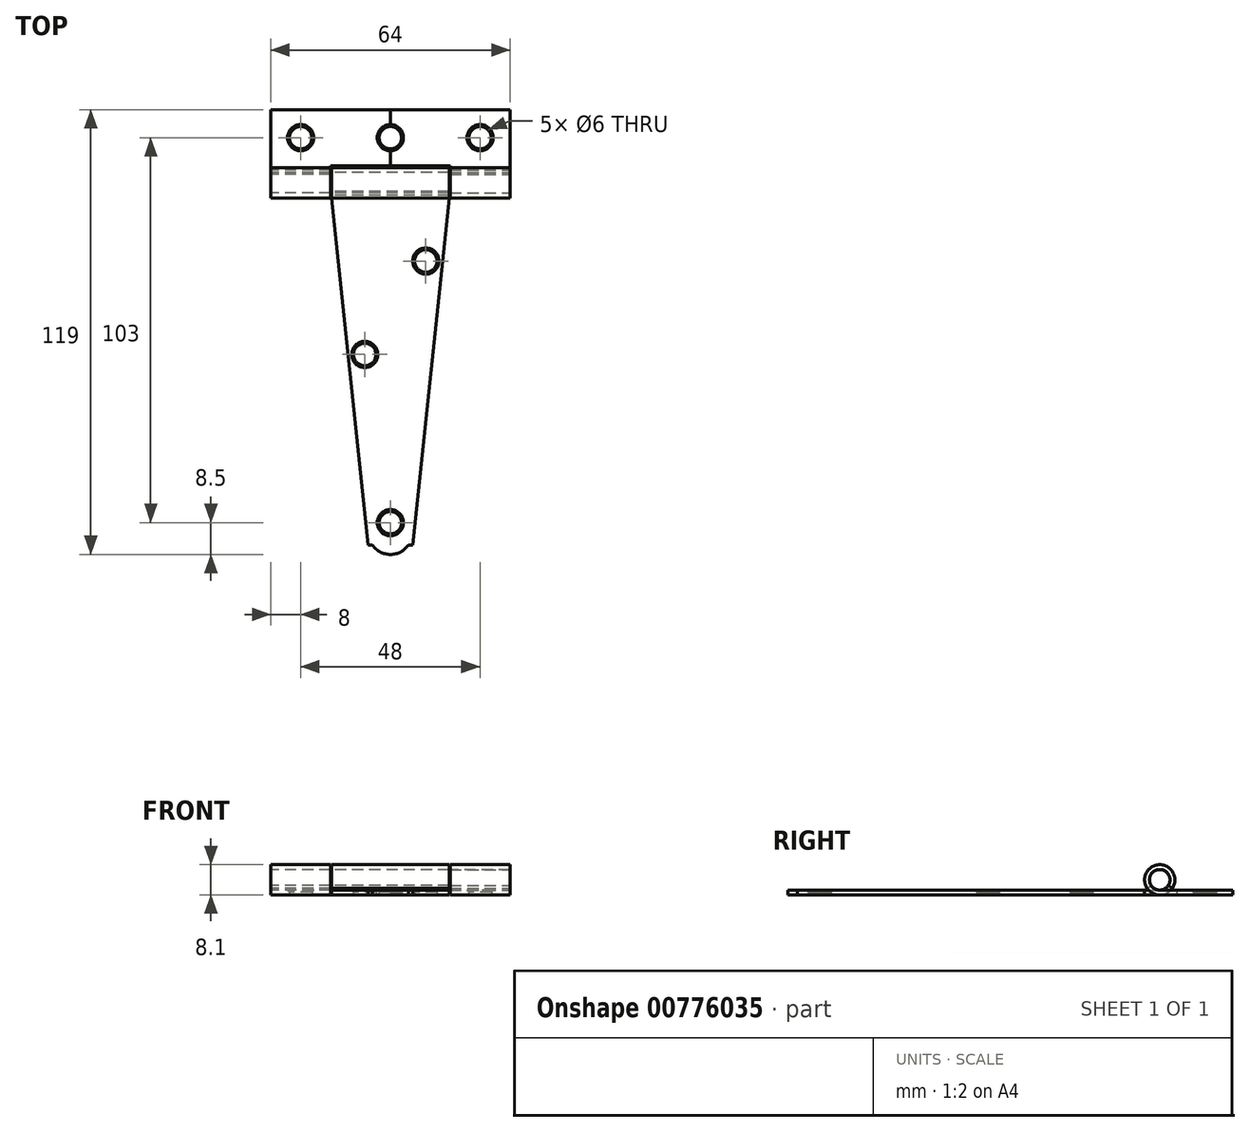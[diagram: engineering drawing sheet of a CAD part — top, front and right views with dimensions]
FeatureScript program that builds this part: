
annotation { "Feature Type Name" : "Feature", "Feature Type Description" : "" }
export const myFeature = defineFeature(function(context is Context, id is Id, definition is map)
    precondition{}
    {
        {
            var Q0;
            Q0=qCreatedBy(makeId("Top.planeOp"),FACE);
            var sketch = newSketch(context, id + "F0", { "sketchPlane" : qUnion([Q0])});
            skLineSegment(sketch, "E0.bottom", {"start": v(-32, 15.5) * mm, "end": v(0, 15.5) * mm});
            skLineSegment(sketch, "E0.top", {"start": v(-32, 0) * mm, "end": v(-16, 0) * mm});
            skLineSegment(sketch, "E0.left", {"start": v(-32, 15.5) * mm, "end": v(-32, 0) * mm});
            skLineSegment(sketch, "E0.right", {"start": v(0, 15.5) * mm, "end": v(0, 11) * mm});
            skLineSegment(sketch, "E1", {"start": v(0, 0.5) * mm, "end": v(-16, 0.5) * mm});
            skLineSegment(sketch, "E2", {"start": v(-16, 0.5) * mm, "end": v(-16, 0) * mm});
            skPoint(sketch, "E3.orphan", {"position": v(0, 0) * mm});
            skArc(sketch, "E4", {"start": v(0, 11) * mm, "mid": v(-3, 8) * mm, "end": v(0, 5) * mm});
            skCircle(sketch, "E5", {"center": v(-24, 8) * mm, "radius": 3 * mm});
            skLineSegment(sketch, "E6", {"start": v(-32, 0) * mm, "end": v(-32, -8.1) * mm, "construction": true});
            skLineSegment(sketch, "E7", {"start": v(-32, -8.1) * mm, "end": v(-16, -8.1) * mm, "construction": true});
            skLineSegment(sketch, "E8", {"start": v(-16, -8.1) * mm, "end": v(-16, 0) * mm, "construction": true});
            skLineSegment(sketch, "E9.trimOffspring", {"start": v(0, 5) * mm, "end": v(0, 0.5) * mm});
            skLineSegment(sketch, "E10", {"start": v(0, 0) * mm, "end": v(-15.75, 0) * mm, "construction": true});
            skLineSegment(sketch, "E11", {"start": v(-15.75, 0) * mm, "end": v(-15.75, -8.1) * mm, "construction": true});
            skLineSegment(sketch, "E12", {"start": v(-15.75, -8.1) * mm, "end": v(0, -8.1) * mm, "construction": true});
            skLineSegment(sketch, "E13", {"start": v(0, -8.1) * mm, "end": v(0, 0) * mm, "construction": true});
            skLineSegment(sketch, "E14", {"start": v(-15.75, -8.1) * mm, "end": v(-6, -101) * mm});
            skLineSegment(sketch, "E15", {"start": v(-6, -101) * mm, "end": v(-4.81, -101) * mm});
            skLineSegment(sketch, "E16", {"start": v(0, 0.5) * mm, "end": v(0, -103.5) * mm});
            skArc(sketch, "E17", {"start": v(-4.81, -101) * mm, "mid": v(-2.71, -102.84) * mm, "end": v(0, -103.5) * mm});
            skCircle(sketch, "E18", {"center": v(0, -95) * mm, "radius": 3 * mm});
            skCircle(sketch, "E19", {"center": v(-6.85, -50) * mm, "radius": 3 * mm});
            skCircle(sketch, "E20", {"center": v(9.48, -25) * mm, "radius": 3 * mm});
            skLineSegment(sketch, "E21", {"start": v(-15.75, -8.1) * mm, "end": v(0, -8.1) * mm});
            skLineSegment(sketch, "E22", {"start": v(-6.85, -50) * mm, "end": v(-11.35, -50) * mm, "construction": true});
            skLineSegment(sketch, "E23.MirrorCS", {"start": v(15.75, -8.1) * mm, "end": v(6, -101) * mm});
            skLineSegment(sketch, "E24", {"start": v(9.48, -25) * mm, "end": v(13.98, -25) * mm, "construction": true});
            skSolve(sketch);
        }
        {
            var Q0;
            Q0=makeQuery(id+"F0.imprint","IMPRINT",FACE,{"disambiguationData":[TD([[makeQuery(id+"F0.imprint","IMPRINT",EDGE,{"derivedFrom":sQuery(id+"F0.wireOp",EDGE,"E0.bottom")}),-1.0]])]});
            extrude(context, id + "F1", {"entities" : qUnion([Q0]), "depth" : 1.3 * mm, "offsetDistance" : 25 * mm});
        }
        {
            var Q0;
            Q0=makeQuery(id+"F0.imprint","IMPRINT",FACE,{"disambiguationData":[TD([[makeQuery(id+"F0.imprint","IMPRINT",EDGE,{"derivedFrom":sQuery(id+"F0.wireOp",EDGE,"E14")}),1.0]])]});
            var Q1;
            Q1=makeQuery(id+"F0.imprint","IMPRINT",FACE,{"disambiguationData":[TD([[makeQuery(id+"F0.imprint","IMPRINT",EDGE,{"derivedFrom":sQuery(id+"F0.wireOp",EDGE,"E19")}),1.0]])]});
            extrude(context, id + "F2", {"entities" : qUnion([Q0, Q1]), "depth" : 1.3 * mm, "offsetDistance" : 25 * mm});
        }
        {
            var Q0;
            Q0=makeQuery(id+"F1.opExtrude","SWEPT_BODY",BODY,{"disambiguationData":[OSD([sQuery(id+"F0.wireOp",EDGE,"E0.bottom"),sQuery(id+"F0.wireOp",EDGE,"E0.top"),sQuery(id+"F0.wireOp",EDGE,"E0.left"),sQuery(id+"F0.wireOp",EDGE,"E0.right"),sQuery(id+"F0.wireOp",EDGE,"E1"),sQuery(id+"F0.wireOp",EDGE,"E2"),sQuery(id+"F0.wireOp",EDGE,"E4"),sQuery(id+"F0.wireOp",EDGE,"E5"),sQuery(id+"F0.wireOp",EDGE,"E9.trimOffspring")])]});
            var Q1;
            {var subQ0=sQuery(id+"F0.wireOp",EDGE,"E16");Q1=makeQuery(id+"F2.opExtrude","SWEPT_FACE",FACE,{"disambiguationData":[OSD([subQ0]),TDD([makeQuery(id+"F0.imprint","IMPRINT",EDGE,{"disambiguationData":[TD([[makeQuery(id+"F0.imprint","INTERSECT",VERTEX,{"derivedFrom":[subQ0,sQuery(id+"F0.wireOp",EDGE,"E21")]}),-1.0]])],"derivedFrom":subQ0})])]});}
            mirror(context, id + "F3", {"operationType" : NewBodyOperationType.ADD, "entities" : qUnion([Q0]), "mirrorPlane" : qUnion([Q1])});
        }
        {
            var Q0;
            Q0=makeQuery(id+"F2.opExtrude","SWEPT_BODY",BODY,{"disambiguationData":[OSD([sQuery(id+"F0.wireOp",EDGE,"E14"),sQuery(id+"F0.wireOp",EDGE,"E15"),sQuery(id+"F0.wireOp",EDGE,"E16"),sQuery(id+"F0.wireOp",EDGE,"E17"),sQuery(id+"F0.wireOp",EDGE,"E18"),sQuery(id+"F0.wireOp",EDGE,"E21")])]});
            var Q1;
            {var subQ0=sQuery(id+"F0.wireOp",EDGE,"E16");Q1=makeQuery(id+"F2.opExtrude","SWEPT_FACE",FACE,{"disambiguationData":[OSD([subQ0]),TDD([makeQuery(id+"F0.imprint","IMPRINT",EDGE,{"disambiguationData":[TD([[makeQuery(id+"F0.imprint","INTERSECT",VERTEX,{"derivedFrom":[subQ0,sQuery(id+"F0.wireOp",EDGE,"E21")]}),-1.0]])],"derivedFrom":subQ0})])]});}
            mirror(context, id + "F4", {"operationType" : NewBodyOperationType.ADD, "entities" : qUnion([Q0]), "mirrorPlane" : qUnion([Q1])});
        }
        {
            var Q0;
            Q0=makeQuery(id+"F0.imprint","IMPRINT",FACE,{"disambiguationData":[TD([[makeQuery(id+"F0.imprint","IMPRINT",EDGE,{"derivedFrom":sQuery(id+"F0.wireOp",EDGE,"E20")}),1.0]])]});
            var Q1;
            Q1=makeQuery(id+"F0.imprint","IMPRINT",FACE,{"disambiguationData":[TD([[makeQuery(id+"F0.imprint","IMPRINT",EDGE,{"derivedFrom":sQuery(id+"F0.wireOp",EDGE,"E19")}),1.0]])]});
            extrude(context, id + "F5", {"entities" : qUnion([Q0, Q1]), "operationType" : NewBodyOperationType.REMOVE, "endBound" : BoundingType.THROUGH_ALL, "depth" : 25 * mm, "offsetDistance" : 25 * mm});
        }
        {
            var Q0;
            Q0=qCreatedBy(makeId("Right.planeOp"),FACE);
            var sketch = newSketch(context, id + "F6", { "sketchPlane" : qUnion([Q0])});
            skPoint(sketch, "E25.0", {"position": v(-8.1, 0) * mm});
            skLineSegment(sketch, "E26.bottom", {"start": v(-8.1, 0) * mm, "end": v(0, 0) * mm, "construction": true});
            skLineSegment(sketch, "E26.top", {"start": v(-8.1, 8.1) * mm, "end": v(0, 8.1) * mm, "construction": true});
            skLineSegment(sketch, "E26.left", {"start": v(-8.1, 0) * mm, "end": v(-8.1, 8.1) * mm, "construction": true});
            skLineSegment(sketch, "E26.right", {"start": v(0, 0) * mm, "end": v(0, 8.1) * mm, "construction": true});
            skLineSegment(sketch, "E27", {"start": v(-4.05, 8.1) * mm, "end": v(-4.05, 0) * mm, "construction": true});
            skArc(sketch, "E28", {"start": v(-4.05, 0) * mm, "mid": v(-2.15, 7.63) * mm, "end": v(-7.4, 1.77) * mm});
            skPoint(sketch, "E29.0", {"position": v(-8.1, 1.3) * mm});
            skLineSegment(sketch, "E30", {"start": v(-8.1, 1.3) * mm, "end": v(-4.05, 1.3) * mm});
            skArc(sketch, "E31", {"start": v(-4.05, 1.3) * mm, "mid": v(-2.76, 6.48) * mm, "end": v(-6.33, 2.5) * mm});
            skLineSegment(sketch, "E32", {"start": v(-7.4, 1.77) * mm, "end": v(-6.33, 2.5) * mm});
            skLineSegment(sketch, "E33", {"start": v(-4.05, 0) * mm, "end": v(-8.1, 0) * mm});
            skLineSegment(sketch, "E34", {"start": v(-8.1, 1.3) * mm, "end": v(-8.1, 0) * mm});
            skSolve(sketch);
        }
        {
            var Q0;
            Q0 = qSketchRegion(id + "F6", true);
            var Q1;
            Q1=makeQuery(id+"F4.opPattern","COPY",VERTEX,{"derivedFrom":makeQuery(id+"F2.opExtrude","CAP_VERTEX",VERTEX,{"disambiguationData":[OSD([sQuery(id+"F0.wireOp",EDGE,"E14"),sQuery(id+"F0.wireOp",EDGE,"E21")])],"isStart":false}),"instanceName":"1"});
            var Q2;
            Q2=makeQuery(id+"F2.opExtrude","CAP_VERTEX",VERTEX,{"disambiguationData":[OSD([sQuery(id+"F0.wireOp",EDGE,"E14"),sQuery(id+"F0.wireOp",EDGE,"E21")])],"isStart":false});
            extrude(context, id + "F7", {"entities" : qUnion([Q0]), "operationType" : NewBodyOperationType.ADD, "endBound" : BoundingType.UP_TO_VERTEX, "depth" : 25 * mm, "endBoundEntityVertex" : qUnion([Q1]), "offsetDistance" : 25 * mm, "hasSecondDirection" : true, "secondDirectionBound" : SecondDirectionBoundingType.UP_TO_VERTEX, "secondDirectionOppositeDirection" : true, "secondDirectionDepth" : 25 * mm, "secondDirectionBoundEntityVertex" : qUnion([Q2])});
        }
        {
            var Q0;
            Q0=makeQuery(id+"F1.opExtrude","SWEPT_FACE",FACE,{"disambiguationData":[OSD([sQuery(id+"F0.wireOp",EDGE,"E0.left")])]});
            var sketch = newSketch(context, id + "F8", { "sketchPlane" : qUnion([Q0])});
            skPoint(sketch, "E35.0", {"position": v(0, 1.3) * mm});
            skPoint(sketch, "E36.0", {"position": v(0, 0) * mm});
            skPoint(sketch, "E37.0", {"position": v(8.1, 0) * mm});
            skLineSegment(sketch, "E38.bottom", {"start": v(0, 0) * mm, "end": v(8.1, 0) * mm, "construction": true});
            skLineSegment(sketch, "E38.top", {"start": v(0, 8.1) * mm, "end": v(8.1, 8.1) * mm, "construction": true});
            skLineSegment(sketch, "E38.left", {"start": v(0, 0) * mm, "end": v(0, 8.1) * mm, "construction": true});
            skLineSegment(sketch, "E38.right", {"start": v(8.1, 0) * mm, "end": v(8.1, 8.1) * mm, "construction": true});
            skLineSegment(sketch, "E39", {"start": v(4.05, 8.1) * mm, "end": v(4.05, 0) * mm, "construction": true});
            skArc(sketch, "E40", {"start": v(4.05, 0) * mm, "mid": v(5.95, 7.63) * mm, "end": v(0.7, 1.77) * mm});
            skLineSegment(sketch, "E41", {"start": v(0, 1.3) * mm, "end": v(4.05, 1.3) * mm});
            skArc(sketch, "E42", {"start": v(4.05, 1.3) * mm, "mid": v(5.34, 6.48) * mm, "end": v(1.77, 2.5) * mm});
            skLineSegment(sketch, "E43", {"start": v(1.77, 2.5) * mm, "end": v(0.7, 1.77) * mm});
            skLineSegment(sketch, "E44", {"start": v(0, 1.3) * mm, "end": v(0, 0) * mm});
            skLineSegment(sketch, "E45", {"start": v(0, 0) * mm, "end": v(4.05, 0) * mm});
            skSolve(sketch);
        }
        {
            var Q0;
            Q0 = qSketchRegion(id + "F8", true);
            var Q1;
            Q1=makeQuery(id+"F1.opExtrude","CAP_VERTEX",VERTEX,{"disambiguationData":[OSD([sQuery(id+"F0.wireOp",EDGE,"E0.top"),sQuery(id+"F0.wireOp",EDGE,"E2")])],"isStart":false});
            extrude(context, id + "F9", {"entities" : qUnion([Q0]), "endBound" : BoundingType.UP_TO_VERTEX, "oppositeDirection" : true, "depth" : 25 * mm, "endBoundEntityVertex" : qUnion([Q1]), "offsetDistance" : 25 * mm});
        }
        {
            var Q0;
            Q0=makeQuery(id+"F9.opExtrude","SWEPT_BODY",BODY,{"disambiguationData":[OSD([sQuery(id+"F8.wireOp",EDGE,"E40"),sQuery(id+"F8.wireOp",EDGE,"E41"),sQuery(id+"F8.wireOp",EDGE,"E42"),sQuery(id+"F8.wireOp",EDGE,"E43"),sQuery(id+"F8.wireOp",EDGE,"E44"),sQuery(id+"F8.wireOp",EDGE,"E45")])]});
            var Q1;
            Q1=qCreatedBy(makeId("Right.planeOp"),FACE);
            mirror(context, id + "F10", {"operationType" : NewBodyOperationType.ADD, "entities" : qUnion([Q0]), "mirrorPlane" : qUnion([Q1])});
        }
        {
            var Q0;
            Q0=makeQuery(id+"F10.boolean.opBoolean","MERGE",FACE,{"derivedFrom":[makeQuery(id+"F1.opExtrude","SWEPT_FACE",FACE,{"disambiguationData":[OSD([sQuery(id+"F0.wireOp",EDGE,"E0.left")])]}),makeQuery(id+"F9.opExtrude","CAP_FACE",FACE,{"disambiguationData":[OSD([sQuery(id+"F8.wireOp",EDGE,"E40"),sQuery(id+"F8.wireOp",EDGE,"E41"),sQuery(id+"F8.wireOp",EDGE,"E42"),sQuery(id+"F8.wireOp",EDGE,"E43"),sQuery(id+"F8.wireOp",EDGE,"E44"),sQuery(id+"F8.wireOp",EDGE,"E45")])],"isStart":true})]});
            var sketch = newSketch(context, id + "F11", { "sketchPlane" : qUnion([Q0])});
            skArc(sketch, "E46.0", {"start": v(4.05, 0) * mm, "mid": v(5.95, 7.63) * mm, "end": v(0.7, 1.77) * mm});
            skCircle(sketch, "E47", {"center": v(4.05, 4.05) * mm, "radius": 2.75 * mm});
            skSolve(sketch);
        }
        {
            var Q0;
            Q0 = qSketchRegion(id + "F11", true);
            var Q1;
            Q1=makeQuery(id+"F10.boolean.opBoolean","MERGE",FACE,{"derivedFrom":[makeQuery(id+"F3.opPattern","COPY",FACE,{"derivedFrom":makeQuery(id+"F1.opExtrude","SWEPT_FACE",FACE,{"disambiguationData":[OSD([sQuery(id+"F0.wireOp",EDGE,"E0.left")])]}),"instanceName":"1"}),makeQuery(id+"F10.opPattern","COPY",FACE,{"derivedFrom":makeQuery(id+"F9.opExtrude","CAP_FACE",FACE,{"disambiguationData":[OSD([sQuery(id+"F8.wireOp",EDGE,"E40"),sQuery(id+"F8.wireOp",EDGE,"E41"),sQuery(id+"F8.wireOp",EDGE,"E42"),sQuery(id+"F8.wireOp",EDGE,"E43"),sQuery(id+"F8.wireOp",EDGE,"E44"),sQuery(id+"F8.wireOp",EDGE,"E45")])],"isStart":true}),"instanceName":"1"})]});
            extrude(context, id + "F12", {"entities" : qUnion([Q0]), "endBound" : BoundingType.UP_TO_SURFACE, "oppositeDirection" : true, "depth" : 25 * mm, "endBoundEntityFace" : qUnion([Q1]), "offsetDistance" : 25 * mm});
        }
        {
            var Q0;
            Q0=makeQuery(id+"F3.opPattern","COPY",EDGE,{"derivedFrom":makeQuery(id+"F1.opExtrude","CAP_EDGE",EDGE,{"disambiguationData":[OSD([sQuery(id+"F0.wireOp",EDGE,"E5")])],"isStart":false}),"instanceName":"1"});
            var Q1;
            {var subQ0=makeQuery(id+"F1.opExtrude","CAP_EDGE",EDGE,{"disambiguationData":[OSD([sQuery(id+"F0.wireOp",EDGE,"E4")])],"isStart":false});Q1=makeQuery(id+"F3.boolean.opBoolean","MERGE",EDGE,{"derivedFrom":[subQ0,makeQuery(id+"F3.opPattern","COPY",EDGE,{"derivedFrom":subQ0,"instanceName":"1"})]});}
            var Q2;
            Q2=makeQuery(id+"F1.opExtrude","CAP_EDGE",EDGE,{"disambiguationData":[OSD([sQuery(id+"F0.wireOp",EDGE,"E5")])],"isStart":false});
            var Q3;
            {var subQ0=makeQuery(id+"F2.opExtrude","CAP_FACE",FACE,{"disambiguationData":[OSD([sQuery(id+"F0.wireOp",EDGE,"E14"),sQuery(id+"F0.wireOp",EDGE,"E15"),sQuery(id+"F0.wireOp",EDGE,"E16"),sQuery(id+"F0.wireOp",EDGE,"E17"),sQuery(id+"F0.wireOp",EDGE,"E18"),sQuery(id+"F0.wireOp",EDGE,"E21")])],"isStart":false});Q3=makeQuery(id+"F5.boolean.opBoolean","INTERSECT",EDGE,{"derivedFrom":[makeQuery(id+"F4.boolean.opBoolean","MERGE",FACE,{"derivedFrom":[subQ0,makeQuery(id+"F4.opPattern","COPY",FACE,{"derivedFrom":subQ0,"instanceName":"1"})]}),makeQuery(id+"F5.opExtrude","SWEPT_FACE",FACE,{"disambiguationData":[OSD([sQuery(id+"F0.wireOp",EDGE,"E20")])]})]});}
            var Q4;
            {var subQ0=makeQuery(id+"F2.opExtrude","CAP_FACE",FACE,{"disambiguationData":[OSD([sQuery(id+"F0.wireOp",EDGE,"E14"),sQuery(id+"F0.wireOp",EDGE,"E15"),sQuery(id+"F0.wireOp",EDGE,"E16"),sQuery(id+"F0.wireOp",EDGE,"E17"),sQuery(id+"F0.wireOp",EDGE,"E18"),sQuery(id+"F0.wireOp",EDGE,"E21")])],"isStart":false});Q4=makeQuery(id+"F5.boolean.opBoolean","INTERSECT",EDGE,{"derivedFrom":[makeQuery(id+"F4.boolean.opBoolean","MERGE",FACE,{"derivedFrom":[subQ0,makeQuery(id+"F4.opPattern","COPY",FACE,{"derivedFrom":subQ0,"instanceName":"1"})]}),makeQuery(id+"F5.opExtrude","SWEPT_FACE",FACE,{"disambiguationData":[OSD([sQuery(id+"F0.wireOp",EDGE,"E19")])]})]});}
            var Q5;
            {var subQ0=makeQuery(id+"F2.opExtrude","CAP_EDGE",EDGE,{"disambiguationData":[OSD([sQuery(id+"F0.wireOp",EDGE,"E18")])],"isStart":false});Q5=makeQuery(id+"F4.boolean.opBoolean","MERGE",EDGE,{"derivedFrom":[subQ0,makeQuery(id+"F4.opPattern","COPY",EDGE,{"derivedFrom":subQ0,"instanceName":"1"})]});}
            chamfer(context, id + "F13", {"entities" : qUnion([Q0, Q1, Q2, Q3, Q4, Q5]), "width" : 0.5 * mm, "tangentPropagation" : true});
        }
    });
